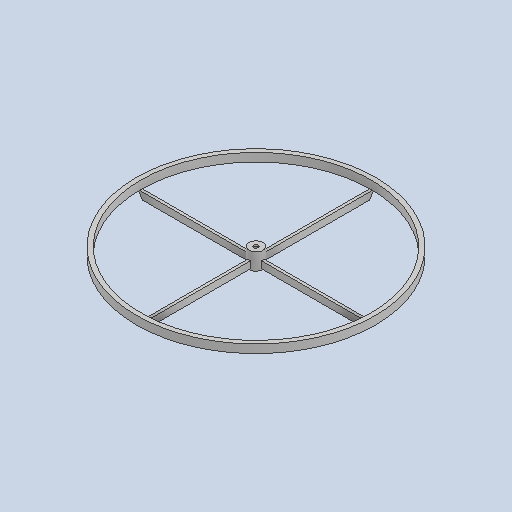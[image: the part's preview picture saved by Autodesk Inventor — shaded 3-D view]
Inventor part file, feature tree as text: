
AUTODESK INVENTOR PART (.ipt)
format: ipt  version: 2023 (Build 270158000, 158)  size: 134,144 bytes
history: imported  units: in
note: dims shown in document units (in); Inventor stores cm internally (conversion verified against a paired STEP export)
features: imported_body x1
ambient origin geometry x8: Origin, YZ Plane, XZ Plane, XY Plane, X Axis, Y Axis, Z Axis, Center Point
bodies: Solid1 (imported_parasolid), Body1 (imported_parasolid)
feature tree (1):
  imported_body  NMx_Import_Brep_tag  [imported B-rep: ~19 faces, bbox_mm=[829.939757, 25.0, 444.494897]]
